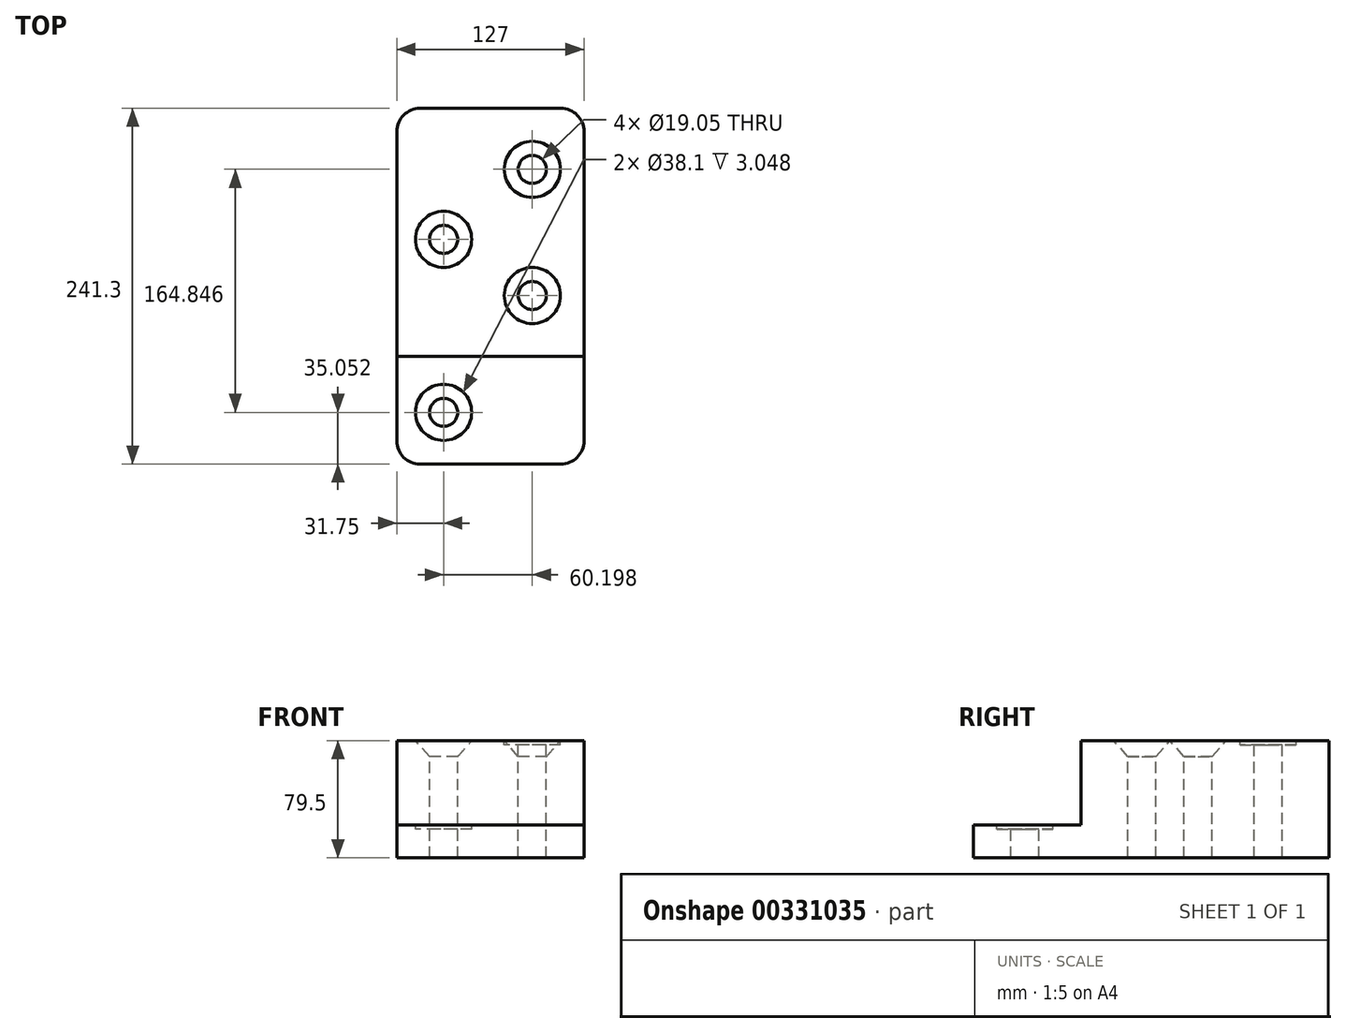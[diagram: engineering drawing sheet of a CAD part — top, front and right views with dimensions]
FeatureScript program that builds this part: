
annotation { "Feature Type Name" : "Feature", "Feature Type Description" : "" }
export const myFeature = defineFeature(function(context is Context, id is Id, definition is map)
    precondition{}
    {
        {
            var Q0;
            Q0=qCreatedBy(makeId("Front.planeOp"),FACE);
            var sketch = newSketch(context, id + "F0", { "sketchPlane" : qUnion([Q0])});
            skLineSegment(sketch, "E0", {"start": v(0, 0) * mm, "end": v(63.5, 0) * mm});
            skLineSegment(sketch, "E1", {"start": v(63.5, 0) * mm, "end": v(63.5, 79.5) * mm});
            skLineSegment(sketch, "E2", {"start": v(63.5, 79.5) * mm, "end": v(-63.5, 79.5) * mm});
            skLineSegment(sketch, "E3", {"start": v(-63.5, 79.5) * mm, "end": v(-63.5, 0) * mm});
            skLineSegment(sketch, "E4", {"start": v(-63.5, 0) * mm, "end": v(0, 0) * mm});
            skSolve(sketch);
        }
        {
            var Q0;
            Q0=makeQuery(id+"F0.imprint","IMPRINT",FACE,{"disambiguationData":[TD([[makeQuery(id+"F0.imprint","IMPRINT",EDGE,{"derivedFrom":sQuery(id+"F0.wireOp",EDGE,"E0")}),1.0]])]});
            extrude(context, id + "F1", {"entities" : qUnion([Q0]), "depth" : 241.3 * mm});
        }
        {
            var Q0;
            Q0=makeQuery(id+"F1.opExtrude","CAP_FACE",FACE,{"disambiguationData":[OSD([sQuery(id+"F0.wireOp",EDGE,"E0"),sQuery(id+"F0.wireOp",EDGE,"E1"),sQuery(id+"F0.wireOp",EDGE,"E2"),sQuery(id+"F0.wireOp",EDGE,"E3"),sQuery(id+"F0.wireOp",EDGE,"E4")])],"isStart":false});
            var sketch = newSketch(context, id + "F2", { "sketchPlane" : qUnion([Q0])});
            skLineSegment(sketch, "E5.0.0", {"start": v(-63.5, 79.5) * mm, "end": v(-63.5, 0) * mm});
            skLineSegment(sketch, "E5.0.1", {"start": v(-63.5, 0) * mm, "end": v(63.5, 0) * mm});
            skLineSegment(sketch, "E5.0.2", {"start": v(63.5, 0) * mm, "end": v(63.5, 79.5) * mm});
            skLineSegment(sketch, "E5.0.3", {"start": v(63.5, 79.5) * mm, "end": v(-63.5, 79.5) * mm});
            skLineSegment(sketch, "E6", {"start": v(63.5, 79.5) * mm, "end": v(63.5, 22.35) * mm});
            skLineSegment(sketch, "E7", {"start": v(63.5, 22.35) * mm, "end": v(-63.5, 22.35) * mm});
            skLineSegment(sketch, "E8", {"start": v(-63.5, 22.35) * mm, "end": v(-63.5, 79.5) * mm});
            skSolve(sketch);
        }
        {
            var Q0;
            Q0=makeQuery(id+"F2.imprint","IMPRINT",FACE,{"disambiguationData":[TD([[makeQuery(id+"F2.imprint","IMPRINT",EDGE,{"derivedFrom":sQuery(id+"F2.wireOp",EDGE,"E5.0.3")}),1.0]])]});
            extrude(context, id + "F3", {"entities" : qUnion([Q0]), "operationType" : NewBodyOperationType.REMOVE, "oppositeDirection" : true, "depth" : 72.9 * mm});
        }
        {
            var Q0;
            Q0=makeQuery(id+"F1.opExtrude","SWEPT_FACE",FACE,{"disambiguationData":[OSD([sQuery(id+"F0.wireOp",EDGE,"E2")])]});
            var sketch = newSketch(context, id + "F4", { "sketchPlane" : qUnion([Q0])});
            skPoint(sketch, "E9", {"position": v(28.45, -127) * mm});
            skPoint(sketch, "E10", {"position": v(28.45, -41.4) * mm});
            skPoint(sketch, "E11", {"position": v(-31.75, -88.9) * mm});
            skSolve(sketch);
        }
        {
            var Q0;
            Q0=sQuery(id+"F4.wireOp",VERTEX,"E10");
            var Q1;
            Q1=makeQuery(id+"F1.opExtrude","SWEPT_BODY",BODY,{"disambiguationData":[OSD([sQuery(id+"F0.wireOp",EDGE,"E0"),sQuery(id+"F0.wireOp",EDGE,"E1"),sQuery(id+"F0.wireOp",EDGE,"E2"),sQuery(id+"F0.wireOp",EDGE,"E3"),sQuery(id+"F0.wireOp",EDGE,"E4")])]});
            hole(context, id + "F5", {"style" : HoleStyle.C_BORE, "endStyle" : HoleEndStyle.THROUGH, "holeDiameter" : 19.05 * mm, "cBoreDiameter" : 38.1 * mm, "cBoreDepth" : 3.05 * mm, "tappedDepth" : 12.7 * mm, "tapClearance" : 3, "locations" : qUnion([Q0]), "scope" : qUnion([Q1])});
        }
        {
            var Q0;
            Q0=sQuery(id+"F4.wireOp",VERTEX,"E11");
            var Q1;
            Q1=sQuery(id+"F4.wireOp",VERTEX,"E9");
            var Q2;
            Q2=makeQuery(id+"F1.opExtrude","SWEPT_BODY",BODY,{"disambiguationData":[OSD([sQuery(id+"F0.wireOp",EDGE,"E0"),sQuery(id+"F0.wireOp",EDGE,"E1"),sQuery(id+"F0.wireOp",EDGE,"E2"),sQuery(id+"F0.wireOp",EDGE,"E3"),sQuery(id+"F0.wireOp",EDGE,"E4")])]});
            hole(context, id + "F6", {"style" : HoleStyle.C_SINK, "endStyle" : HoleEndStyle.THROUGH, "holeDiameter" : 19.05 * mm, "cSinkDiameter" : 38.1 * mm, "cSinkAngle" : 82 * degree, "tappedDepth" : 12.7 * mm, "tapClearance" : 3, "locations" : qUnion([Q0, Q1]), "scope" : qUnion([Q2])});
        }
        {
            var Q0;
            Q0=makeQuery(id+"F3.boolean.opBoolean","COPY",FACE,{"derivedFrom":makeQuery(id+"F3.opExtrude","SWEPT_FACE",FACE,{"disambiguationData":[OSD([sQuery(id+"F2.wireOp",EDGE,"E7")])]})});
            var sketch = newSketch(context, id + "F7", { "sketchPlane" : qUnion([Q0])});
            skPoint(sketch, "E12", {"position": v(-31.75, -206.25) * mm});
            skSolve(sketch);
        }
        {
            var Q0;
            Q0=sQuery(id+"F7.wireOp",VERTEX,"E12");
            var Q1;
            Q1=makeQuery(id+"F1.opExtrude","SWEPT_BODY",BODY,{"disambiguationData":[OSD([sQuery(id+"F0.wireOp",EDGE,"E0"),sQuery(id+"F0.wireOp",EDGE,"E1"),sQuery(id+"F0.wireOp",EDGE,"E2"),sQuery(id+"F0.wireOp",EDGE,"E3"),sQuery(id+"F0.wireOp",EDGE,"E4")])]});
            hole(context, id + "F8", {"style" : HoleStyle.C_BORE, "endStyle" : HoleEndStyle.THROUGH, "holeDiameter" : 19.05 * mm, "cBoreDiameter" : 38.1 * mm, "cBoreDepth" : 3.05 * mm, "tappedDepth" : 12.7 * mm, "tapClearance" : 3, "locations" : qUnion([Q0]), "scope" : qUnion([Q1])});
        }
        {
            var Q0;
            Q0=makeQuery(id+"F3.boolean.opBoolean","COPY",EDGE,{"derivedFrom":makeQuery(id+"F3.opExtrude","CAP_EDGE",EDGE,{"disambiguationData":[OSD([sQuery(id+"F2.wireOp",EDGE,"E6")])],"isStart":false})});
            var Q1;
            Q1=makeQuery(id+"F3.boolean.opBoolean","COPY",EDGE,{"derivedFrom":makeQuery(id+"F3.opExtrude","CAP_EDGE",EDGE,{"disambiguationData":[OSD([sQuery(id+"F2.wireOp",EDGE,"E8")])],"isStart":false})});
            var Q2;
            Q2=makeQuery(id+"F1.opExtrude","CAP_EDGE",EDGE,{"disambiguationData":[OSD([sQuery(id+"F0.wireOp",EDGE,"E3")])],"isStart":false});
            var Q3;
            Q3=makeQuery(id+"F1.opExtrude","CAP_EDGE",EDGE,{"disambiguationData":[OSD([sQuery(id+"F0.wireOp",EDGE,"E1")])],"isStart":false});
            var Q4;
            Q4=makeQuery(id+"F1.opExtrude","CAP_EDGE",EDGE,{"disambiguationData":[OSD([sQuery(id+"F0.wireOp",EDGE,"E1")])],"isStart":true});
            var Q5;
            Q5=makeQuery(id+"F1.opExtrude","CAP_EDGE",EDGE,{"disambiguationData":[OSD([sQuery(id+"F0.wireOp",EDGE,"E3")])],"isStart":true});
            fillet(context, id + "F9", {"entities" : qUnion([Q0, Q1, Q2, Q3, Q4, Q5]), "radius" : 15.75 * mm, "tangentPropagation" : true, "allowEdgeOverflow" : false});
        }
    });
